# Revit family: Sanitary_Showers_hansgrohe_24337XXX-hansgrohe-Shower-arm-E-39-cm_NEW
name_source: partatom
category: Plumbing Fixtures
units: mm (PartAtom-declared; Revit-internal decimal feet)

## family parameters
Always vertical = No
Cut with Voids When Loaded = No
Maintain Annotation Orientation = No
OmniClass Number = 23.31.17.00
OmniClass Title = Showers
Part Type = Normal
Room Calculation Point = No
Round Connector Dimension = Use Diameter
Shared = No
Work Plane-Based = Yes

## types (1)
- Default - please load Revit Family Type Catalog
    Connector Description = Water Inlet 12.7 mm
    Date Updated = 2024/12/26
    Default Elevation = 1219 mm
    Description = hansgrohe Shower arm E 39 cm
    Diameter = 13 mm
    Manufacturer = Hansgrohe
    Material 1 = Hansgrohe - Metal - 000 Chrome
    Model = 24337XXX
    Product Page URL = https://www.hansgrohe.com
    Product data url = https://bimobject.com
    URL = https://www.hansgrohe.com
    Version = 2

## geometry (parser evidence)
native form markers: Sweep x2
no freeform markers — native parametric forms only
